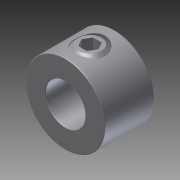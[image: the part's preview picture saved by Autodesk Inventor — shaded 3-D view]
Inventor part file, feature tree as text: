
AUTODESK INVENTOR PART (.ipt)
format: ipt  version: 2015 (Build 190159000, 159)  size: 178,688 bytes
history: native  units: in
note: dims shown in document units (in); Inventor stores cm internally (conversion verified against a paired STEP export)
features: other x2, imported_body x2, fillet x1
ambient origin geometry x8: Origin, YZ Plane, XZ Plane, XY Plane, X Axis, Y Axis, Z Axis, Center Point
bodies: Body1 (feature_tree), Body2 (feature_tree)
feature tree (5):
  fillet  "Fillet1"  [1 undecoded]
  other  "9946K1101"
  other  "Cut-Extrude2"
  imported_body  "Base1"
  imported_body  "Base2"
note: 1 required parameter value undecoded (feature->parameter linkage not recoverable at this tier; creation-order binding heuristic only, values carry confidence <= 0.55)
